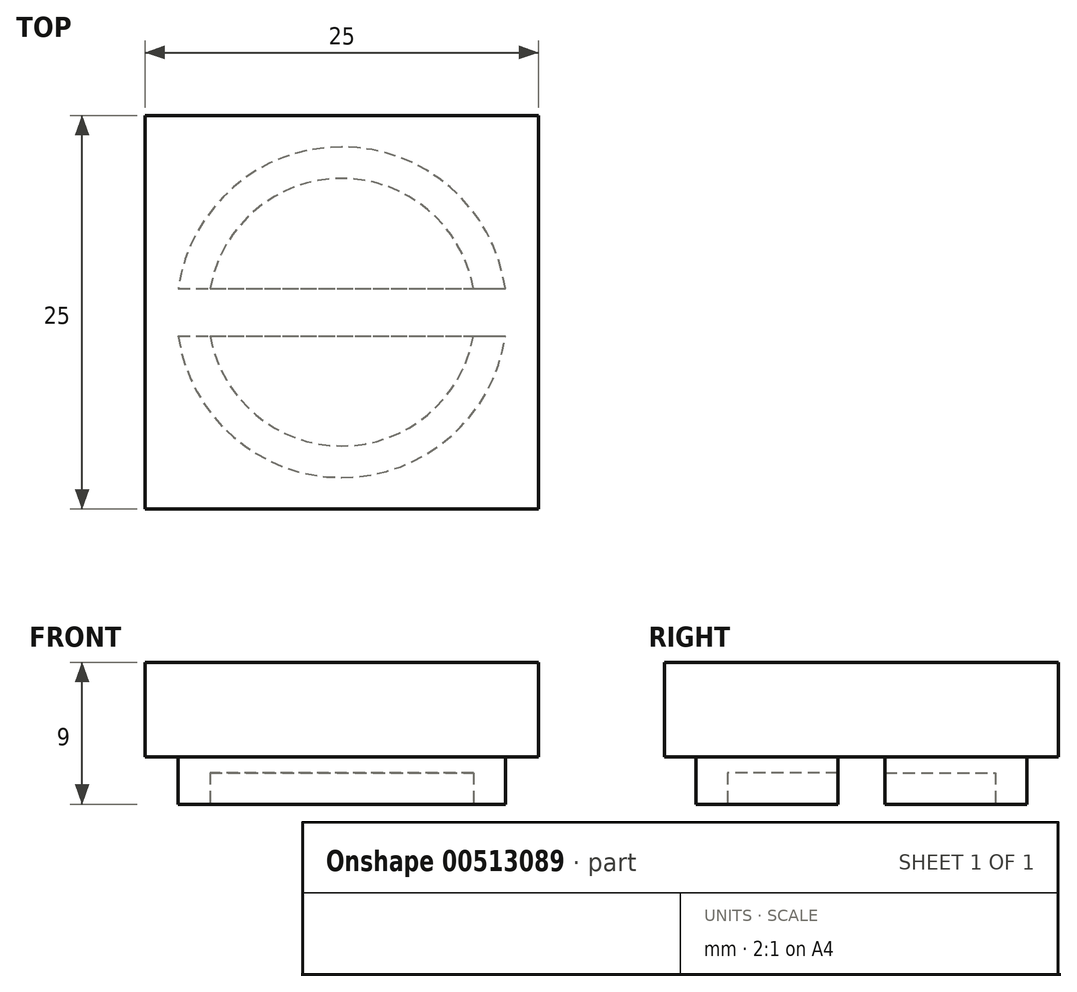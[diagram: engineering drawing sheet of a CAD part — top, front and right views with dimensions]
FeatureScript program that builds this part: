
annotation { "Feature Type Name" : "Feature", "Feature Type Description" : "" }
export const myFeature = defineFeature(function(context is Context, id is Id, definition is map)
    precondition{}
    {
        {
            var Q0;
            Q0=qCreatedBy(makeId("Top.planeOp"),FACE);
            var sketch = newSketch(context, id + "F0", { "sketchPlane" : qUnion([Q0])});
            skLineSegment(sketch, "E0.bottom", {"start": v(12.5, -12.5) * mm, "end": v(-12.5, -12.5) * mm});
            skLineSegment(sketch, "E0.top", {"start": v(12.5, 12.5) * mm, "end": v(-12.5, 12.5) * mm});
            skLineSegment(sketch, "E0.left", {"start": v(12.5, -12.5) * mm, "end": v(12.5, 12.5) * mm});
            skLineSegment(sketch, "E0.right", {"start": v(-12.5, -12.5) * mm, "end": v(-12.5, 12.5) * mm});
            skPoint(sketch, "E0.middle", {"position": v(0, 0) * mm});
            skSolve(sketch);
        }
        {
            var Q0;
            Q0=makeQuery(id+"F0.imprint","IMPRINT",FACE,{"disambiguationData":[TD([[makeQuery(id+"F0.imprint","IMPRINT",EDGE,{"derivedFrom":sQuery(id+"F0.wireOp",EDGE,"E0.bottom")}),-1.0]])]});
            extrude(context, id + "F1", {"entities" : qUnion([Q0]), "flatOperationType" : FlatOperationType.REMOVE, "depth" : 2 * mm + 4 * mm, "offsetDistance" : 25 * mm, "domain" : OperationDomain.MODEL});
        }
        {
            var Q0;
            Q0=makeQuery(id+"F1.opExtrude","CAP_FACE",FACE,{"disambiguationData":[OSD([sQuery(id+"F0.wireOp",EDGE,"E0.bottom"),sQuery(id+"F0.wireOp",EDGE,"E0.top"),sQuery(id+"F0.wireOp",EDGE,"E0.left"),sQuery(id+"F0.wireOp",EDGE,"E0.right")])],"isStart":true});
            var sketch = newSketch(context, id + "F2", { "sketchPlane" : qUnion([Q0])});
            skCircle(sketch, "E1", {"center": v(0, 0) * mm, "radius": 10.5 * mm});
            skSolve(sketch);
        }
        {
            var Q0;
            Q0 = qSketchRegion(id + "F2", true);
            extrude(context, id + "F3", {"entities" : qUnion([Q0]), "operationType" : NewBodyOperationType.ADD, "depth" : 3 * mm, "offsetDistance" : 25 * mm});
        }
        {
            var Q0;
            Q0=makeQuery(id+"F3.opExtrude","CAP_FACE",FACE,{"disambiguationData":[OSD([sQuery(id+"F2.wireOp",EDGE,"E1")])],"isStart":false});
            var sketch = newSketch(context, id + "F4", { "sketchPlane" : qUnion([Q0])});
            skCircle(sketch, "E2", {"center": v(0, 0) * mm, "radius": 8.5 * mm});
            skSolve(sketch);
        }
        {
            var Q0;
            Q0=makeQuery(id+"F4.imprint","IMPRINT",FACE,{"disambiguationData":[TD([[makeQuery(id+"F4.imprint","IMPRINT",EDGE,{"derivedFrom":sQuery(id+"F4.wireOp",EDGE,"E2")}),1.0]])]});
            extrude(context, id + "F5", {"entities" : qUnion([Q0]), "operationType" : NewBodyOperationType.REMOVE, "oppositeDirection" : true, "depth" : 2 * mm, "offsetDistance" : 25 * mm});
        }
        {
            var Q0;
            Q0=qCreatedBy(makeId("Right.planeOp"),FACE);
            var sketch = newSketch(context, id + "F6", { "sketchPlane" : qUnion([Q0])});
            skLineSegment(sketch, "E3.bottom", {"start": v(1.5, -5) * mm, "end": v(-1.5, -5) * mm});
            skLineSegment(sketch, "E3.top", {"start": v(1.5, 0) * mm, "end": v(-1.5, 0) * mm});
            skLineSegment(sketch, "E3.left", {"start": v(1.5, -5) * mm, "end": v(1.5, 0) * mm});
            skLineSegment(sketch, "E3.right", {"start": v(-1.5, -5) * mm, "end": v(-1.5, 0) * mm});
            skPoint(sketch, "E3.middle", {"position": v(0, -2.5) * mm});
            skSolve(sketch);
        }
        {
            var Q0;
            Q0=makeQuery(id+"F6.imprint","IMPRINT",FACE,{"disambiguationData":[TD([[makeQuery(id+"F6.imprint","IMPRINT",EDGE,{"derivedFrom":sQuery(id+"F6.wireOp",EDGE,"E3.bottom")}),-1.0]])]});
            extrude(context, id + "F7", {"entities" : qUnion([Q0]), "operationType" : NewBodyOperationType.REMOVE, "oppositeDirection" : true, "depth" : 25 * mm, "offsetDistance" : 25 * mm, "hasSecondDirection" : true, "secondDirectionOppositeDirection" : false, "secondDirectionDepth" : 25 * mm});
        }
    });
